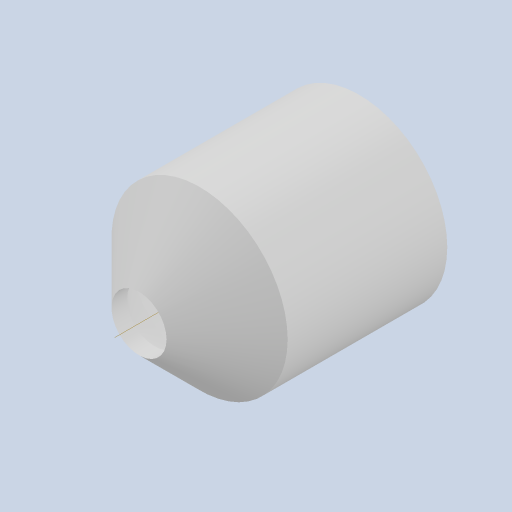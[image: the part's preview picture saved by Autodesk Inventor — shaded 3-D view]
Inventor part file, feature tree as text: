
AUTODESK INVENTOR PART (.ipt)
format: ipt  version: 2023 (Build 270158000, 158)  size: 289,792 bytes
history: native  units: in
note: dims shown in document units (in); Inventor stores cm internally (conversion verified against a paired STEP export)
features: sketch x5, extrude x3, chamfer x1, shell x1, other x1, helix x1
ambient origin geometry x8: Origin, YZ Plane, XZ Plane, XY Plane, X Axis, Y Axis, Z Axis, Center Point
bodies: Solid1 (feature_tree)
feature tree (12):
  extrude  "Extrusion1"  Depth=0.0787in TaperAngle=0.0deg
  chamfer  "Chamfer1"  Distance=0.0787in Angle=45.0deg
  shell  "Shell1"  Thickness=0.0787in
  extrude  "Extrusion2"  Depth=0.0787in
  sketch  "Sketch3"  dims[d11=0.0197in]
  other  "Work Axis1"
  helix  "Coil1"  [1 undecoded]
  extrude  "Extrusion3"  Depth=0.3937in TaperAngle=0.0deg
  sketch  "Sketch5"  dims[d22=0.0197in d23=0.0344in d24=0.0197in d25=0.0344in]
  sketch  "Sketch1"  dims[d0=1.2598in d1=1.5748in d2=0.0in d3=0.4331in d4=0.0787in d5=45.0deg d6=0.0787in]
  sketch  "Sketch2"  dims[d7=1.5748in d8=0.0in d9=0.0787in d10=0.0157in]
  sketch  "Sketch4"  dims[d12=0.0787in d13=0.8268in d14=0.3937in d15=0.0in d16=90.0deg d17=90.0deg d18=0.0in d19=0.0in d20=1.5748in d21=0.0in]
note: 1 required parameter value undecoded (feature->parameter linkage not recoverable at this tier; creation-order binding heuristic only, values carry confidence <= 0.55)
